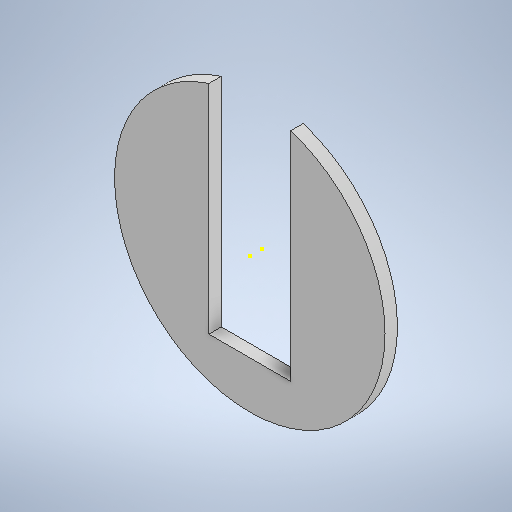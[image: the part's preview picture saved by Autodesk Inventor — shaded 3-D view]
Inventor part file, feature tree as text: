
AUTODESK INVENTOR PART (.ipt)
format: ipt  version: 2025 (Build 290162000, 162)  size: 239,616 bytes
history: native  units: in
note: dims shown in document units (in); Inventor stores cm internally (conversion verified against a paired STEP export)
features: sketch x3, extrude x1
ambient origin geometry x8: Origin, YZ Plane, XZ Plane, XY Plane, X Axis, Y Axis, Z Axis, Center Point
bodies: Solid1 (feature_tree)
feature tree (4):
  extrude  "Extrusion1"  Depth=0.4528in
  sketch  "Sketch2"  dims[d2=1.2008in]
  sketch  "Sketch3"  dims[d3=1.2008in d4=0.0689in d5=0.0in d6=0.0197in d7=0.0344in]
  sketch  "Sketch1"  dims[d0=1.4961in d1=0.4528in]
